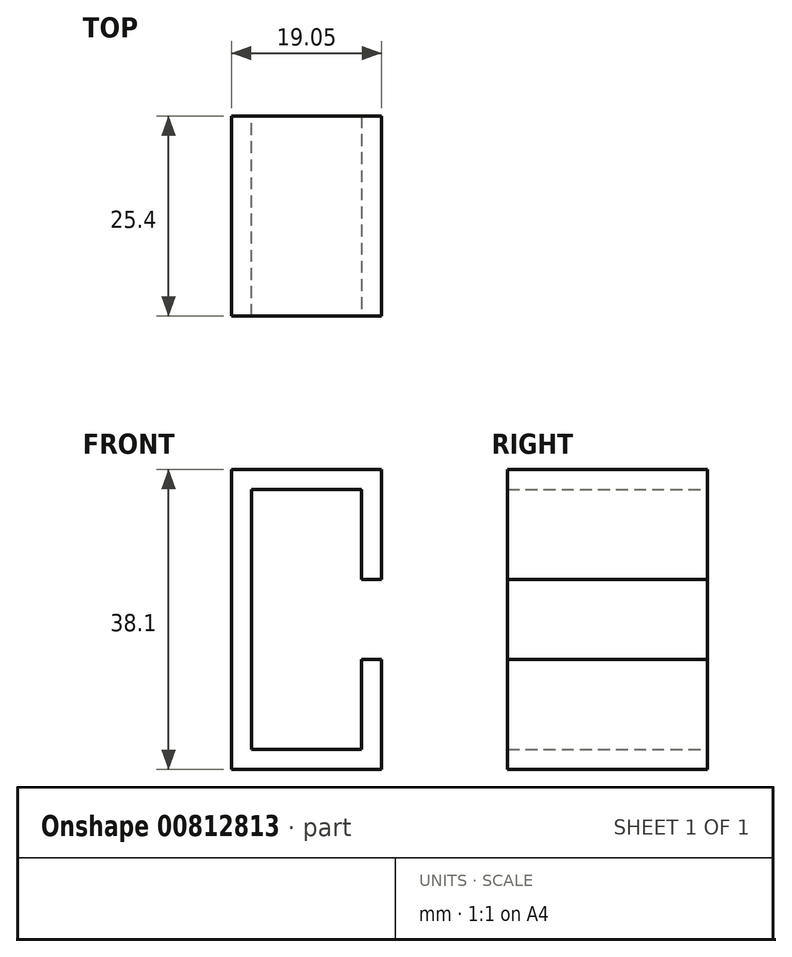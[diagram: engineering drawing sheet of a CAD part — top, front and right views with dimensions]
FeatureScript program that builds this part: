
annotation { "Feature Type Name" : "Feature", "Feature Type Description" : "" }
export const myFeature = defineFeature(function(context is Context, id is Id, definition is map)
    precondition{}
    {
        {
            var Q0;
            Q0=qCreatedBy(makeId("Front.planeOp"),FACE);
            var sketch = newSketch(context, id + "F0", { "sketchPlane" : qUnion([Q0])});
            skLineSegment(sketch, "E0", {"start": v(0, 8.9) * mm, "end": v(0, 19.05) * mm});
            skLineSegment(sketch, "E1", {"start": v(0, 19.05) * mm, "end": v(-19.05, 19.05) * mm});
            skLineSegment(sketch, "E2", {"start": v(-19.05, 19.05) * mm, "end": v(-19.05, 0) * mm});
            skLineSegment(sketch, "E3", {"start": v(-19.05, 0) * mm, "end": v(-19.05, -19.05) * mm});
            skLineSegment(sketch, "E4", {"start": v(-19.05, -19.05) * mm, "end": v(0, -19.05) * mm});
            skLineSegment(sketch, "E5", {"start": v(0, -19.05) * mm, "end": v(0, -8.89) * mm});
            skLineSegment(sketch, "E6", {"start": v(0, 8.9) * mm, "end": v(0, -8.89) * mm});
            skSolve(sketch);
        }
        {
            var Q0;
            Q0=makeQuery(id+"F0.imprint","IMPRINT",FACE,{"disambiguationData":[TD([[makeQuery(id+"F0.imprint","IMPRINT",EDGE,{"derivedFrom":sQuery(id+"F0.wireOp",EDGE,"E0")}),1.0]])]});
            extrude(context, id + "F1", {"entities" : qUnion([Q0]), "depth" : 25.4 * mm, "offsetDistance" : 25.4 * mm});
        }
        {
            var Q0;
            Q0=makeQuery(id+"F1.opExtrude","CAP_FACE",FACE,{"disambiguationData":[OSD([sQuery(id+"F0.wireOp",EDGE,"E0"),sQuery(id+"F0.wireOp",EDGE,"E1"),sQuery(id+"F0.wireOp",EDGE,"E2"),sQuery(id+"F0.wireOp",EDGE,"E3"),sQuery(id+"F0.wireOp",EDGE,"E4"),sQuery(id+"F0.wireOp",EDGE,"E5"),sQuery(id+"F0.wireOp",EDGE,"E6")])],"isStart":false});
            shell(context, id + "F2", {"entities" : qUnion([Q0]), "thickness" : 2.54 * mm});
        }
        {
            var Q0;
            Q0=makeQuery(id+"F2.opShell","OFFSET_FACE",FACE,{"disambiguationData":[OSD([sQuery(id+"F0.wireOp",EDGE,"E0"),sQuery(id+"F0.wireOp",EDGE,"E1"),sQuery(id+"F0.wireOp",EDGE,"E2"),sQuery(id+"F0.wireOp",EDGE,"E3"),sQuery(id+"F0.wireOp",EDGE,"E4"),sQuery(id+"F0.wireOp",EDGE,"E5"),sQuery(id+"F0.wireOp",EDGE,"E6")])]});
            extrude(context, id + "F3", {"entities" : qUnion([Q0]), "operationType" : NewBodyOperationType.REMOVE, "oppositeDirection" : true, "depth" : 25.4 * mm, "offsetDistance" : 25.4 * mm});
        }
        {
            var Q0;
            Q0=makeQuery(id+"F1.opExtrude","CAP_FACE",FACE,{"disambiguationData":[OSD([sQuery(id+"F0.wireOp",EDGE,"E0"),sQuery(id+"F0.wireOp",EDGE,"E1"),sQuery(id+"F0.wireOp",EDGE,"E2"),sQuery(id+"F0.wireOp",EDGE,"E3"),sQuery(id+"F0.wireOp",EDGE,"E4"),sQuery(id+"F0.wireOp",EDGE,"E5"),sQuery(id+"F0.wireOp",EDGE,"E6")])],"isStart":false});
            var sketch = newSketch(context, id + "F4", { "sketchPlane" : qUnion([Q0])});
            skLineSegment(sketch, "E7", {"start": v(-2.54, 5.08) * mm, "end": v(0, 5.08) * mm});
            skLineSegment(sketch, "E8", {"start": v(-2.54, -5.08) * mm, "end": v(0, -5.08) * mm});
            skSolve(sketch);
        }
        {
            var Q0;
            Q0 = qSketchRegion(id + "F4", true);
            var Q1;
            {var subQ0=sQuery(id+"F4.wireOp",EDGE,"E7");Q1=makeQuery(id+"F4.imprint","IMPRINT",FACE,{"disambiguationData":[TD([[makeQuery(id+"F4.imprint","IMPRINT",EDGE,{"derivedFrom":subQ0}),-1.0]])]});}
            extrude(context, id + "F5", {"entities" : qUnion([Q0, Q1]), "operationType" : NewBodyOperationType.REMOVE, "oppositeDirection" : true, "depth" : 25.4 * mm, "offsetDistance" : 25.4 * mm});
        }
    });
